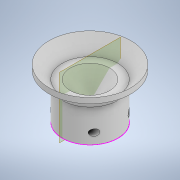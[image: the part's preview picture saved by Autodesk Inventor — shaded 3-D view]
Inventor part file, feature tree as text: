
AUTODESK INVENTOR PART (.ipt)
format: ipt  version: 2020 (Build 240168000, 168)  size: 176,128 bytes
history: native  units: in
note: dims shown in document units (in); Inventor stores cm internally (conversion verified against a paired STEP export)
features: sketch x4, hole x2, revolve x1, plane x1
ambient origin geometry x8: Origin, YZ Plane, XZ Plane, XY Plane, X Axis, Y Axis, Z Axis, Center Point
bodies: Solid1 (feature_tree)
feature tree (8):
  revolve  "Revolution1"  [1 undecoded]
  hole  "Hole1"  [1 undecoded]
  sketch  "Sketch3"  dims[d16=45.0deg d17=90.0deg]
  plane  "Work Plane1"
  hole  "Hole2"  [1 undecoded]
  sketch  "Sketch1"  dims[d7=90.0deg d8=0.211in]
  sketch  "Sketch2"  dims[d10=0.375in d11=0.25in d12=0.5635in d13=0.375in d14=0.0in d15=0.325in]
  sketch  "Sketch4"  dims[d18=0.4in d19=45.0deg d20=0.4in d21=135.0deg d22=0.177in d23=0.328in d24=0.332in d25=0.25in d26=0.5635in d27=0.484in d28=0.8108in d29=0.725in d30=0.389in d31=45.0deg d32=0.5in d33=45.0deg d34=0.146in d35=180.0deg]
note: 3 required parameter values undecoded (feature->parameter linkage not recoverable at this tier; creation-order binding heuristic only, values carry confidence <= 0.55)